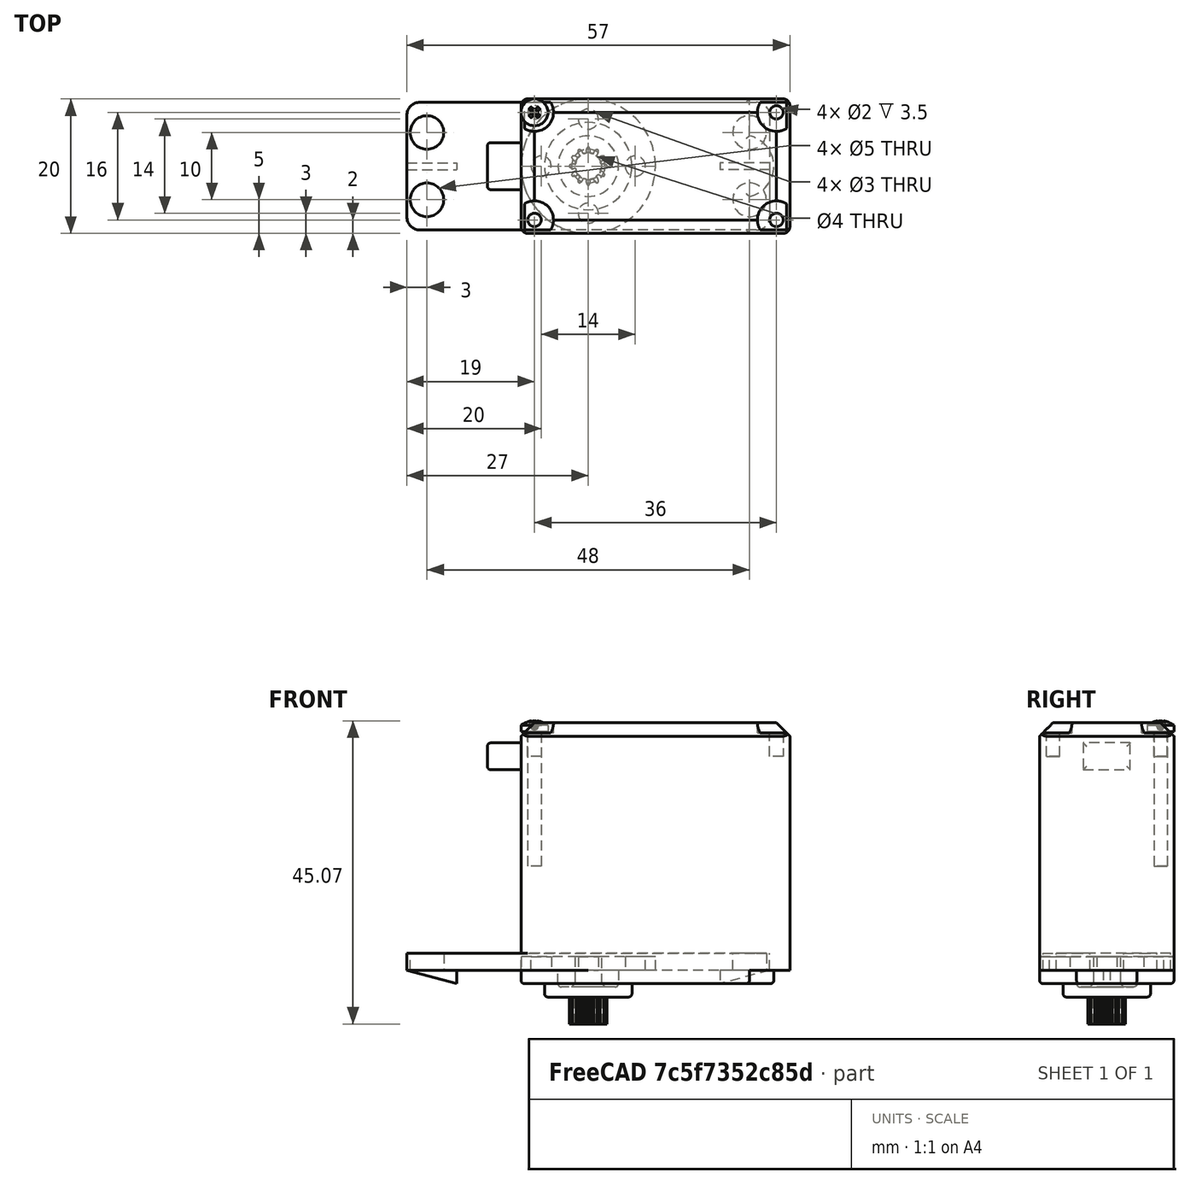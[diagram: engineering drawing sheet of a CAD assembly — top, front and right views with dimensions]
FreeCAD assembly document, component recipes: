
FREECAD ASSEMBLY — COMPONENT RECIPES ("Servo")

This assembly document has 3 components, labeled P0..P2 below (a component is one placed body or linked part). 3 of them carry a construction recipe — the FreeCAD feature program that regenerates the part from scratch, quoted from this document or its linked companion documents; the rest are supplied as boundary geometry only. No exploded tour is included for this assembly.
COMPONENT P0 — recipe-attached ("Hang", modeled in this document).
Construction recipe (the document's own serialized feature program — sketch geometry with constraints, then the solid features built on it; lengths are millimeters unless a unit is written):

FEATURE [PartDesign::CoordinateSystem] LCS_0002
  AttacherType = Attacher::AttachEngine3D
  MapMode = 2
  Support = -> [X_Axis002]
FEATURE [Sketcher::SketchObject] Sketch008
  FullyConstrained = true
  MapMode = 5
  Support = -> [XY_Plane002]
  sketch-geometry (4):
    g0: LineSegment StartX=-27 StartY=9.5 StartZ=0 EndX=27 EndY=9.5 EndZ=0
    g1: LineSegment StartX=27 StartY=9.5 StartZ=0 EndX=27 EndY=-9.5 EndZ=0
    g2: LineSegment StartX=27 StartY=-9.5 StartZ=0 EndX=-27 EndY=-9.5 EndZ=0
    g3: LineSegment StartX=-27 StartY=-9.5 StartZ=0 EndX=-27 EndY=9.5 EndZ=0
  constraints (11):
    c: Coincident(g0,g1)
    c: Coincident(g1,g2)
    c: Coincident(g2,g3)
    c: Coincident(g3,g0)
    c: Horizontal(g0)
    c: Horizontal(g2)
    c: Vertical(g1)
    c: Vertical(g3)
    c: Symmetric(g0,g1,g-1)
    c: Distance(g0) = 54
    c: Distance(g1) = 19
FEATURE [PartDesign::Pad] Pad006
  Direction = (1,1,1)
  Length = 2.5
  Length2 = 100
  Profile = -> Sketch008
  Type = 0
FEATURE [Sketcher::SketchObject] Sketch009
  FullyConstrained = true
  MapMode = 5
  Placement = pos=(0,0,2.5) rot=(0,0,1;0rad)
  Support = -> [Pad006]
  sketch-geometry (8):
    g0: LineSegment StartX=-24 StartY=5 StartZ=0 EndX=24 EndY=5 EndZ=0
    g1: LineSegment StartX=24 StartY=5 StartZ=0 EndX=24 EndY=-5 EndZ=0
    g2: LineSegment StartX=24 StartY=-5 StartZ=0 EndX=-24 EndY=-5 EndZ=0
    g3: LineSegment StartX=-24 StartY=-5 StartZ=0 EndX=-24 EndY=5 EndZ=0
    g4: Circle CenterX=-24 CenterY=5 CenterZ=0 NormalX=0 NormalY=0 NormalZ=1 AngleXU=0 Radius=2.5
    g5: Circle CenterX=24 CenterY=5 CenterZ=0 NormalX=0 NormalY=0 NormalZ=1 AngleXU=0 Radius=2.5
    g6: Circle CenterX=24 CenterY=-5 CenterZ=0 NormalX=0 NormalY=0 NormalZ=1 AngleXU=0 Radius=2.5
    g7: Circle CenterX=-24 CenterY=-5 CenterZ=0 NormalX=0 NormalY=0 NormalZ=1 AngleXU=0 Radius=2.5
  constraints (19):
    c: Coincident(g0,g1)
    c: Coincident(g1,g2)
    c: Coincident(g2,g3)
    c: Coincident(g3,g0)
    c: Horizontal(g0)
    c: Horizontal(g2)
    c: Vertical(g1)
    c: Vertical(g3)
    c: Symmetric(g0,g1,g-1)
    c: Distance(g0) = 48
    c: Distance(g1) = 10
    c: Coincident(g4,g0)
    c: Coincident(g5,g0)
    c: Coincident(g6,g1)
    c: Coincident(g7,g2)
    c: Diameter(g4) = 5
    c: Diameter(g5) = 5
    c: Diameter(g6) = 5
    c: Diameter(g7) = 5
FEATURE [PartDesign::Pocket] Pocket002
  BaseFeature = -> Pad006
  Length = 5
  Length2 = 100
  Profile = -> Sketch009
  Type = 1
FEATURE [PartDesign::Fillet] Fillet007
  Base = -> Pocket002 [Edge2]
  BaseFeature = -> Pocket002
  Radius = 2
  SupportTransform = false
FEATURE [PartDesign::Fillet] Fillet008
  Base = -> Fillet007 [Edge3]
  BaseFeature = -> Fillet007
  Radius = 2
  SupportTransform = false
FEATURE [PartDesign::Fillet] Fillet009
  Base = -> Fillet008 [Edge25]
  BaseFeature = -> Fillet008
  Radius = 2
  SupportTransform = false
FEATURE [PartDesign::Fillet] Fillet010
  Base = -> Fillet009 [Edge19]
  BaseFeature = -> Fillet009
  Radius = 2
  SupportTransform = false
FEATURE [Sketcher::SketchObject] Sketch010
  ExternalGeometry = -> [Fillet010]
  FullyConstrained = true
  MapMode = 5
  Placement = pos=(0,0,0) rot=(1,0,0;1.5708rad)
  Support = -> [XZ_Plane002]
  sketch-geometry (3):
    g0: LineSegment StartX=-27 StartY=0 StartZ=0 EndX=-19.6 EndY=0 EndZ=0
    g1: LineSegment StartX=-19.6 StartY=0 StartZ=0 EndX=-19.6 EndY=-2 EndZ=0
    g2: LineSegment StartX=-27 StartY=0 StartZ=0 EndX=-19.6 EndY=-2 EndZ=0
  constraints (9):
    c: PointOnObject(g0,g-1)
    c: Horizontal(g0)
    c: Vertical(g1)
    c: Coincident(g2,g0)
    c: Coincident(g2,g1)
    c: Distance(g1) = 2
    c: Distance(g0) = 7.4
    c: Coincident(g0,g1)
    c: DistanceX(g-3,g0) = 0
FEATURE [PartDesign::Pad] Pad007
  BaseFeature = -> Fillet010
  Direction = (1,1,1)
  Length = 1
  Length2 = 100
  Midplane = true
  Profile = -> Sketch010
  Type = 0
FEATURE [PartDesign::Mirrored] Mirrored
  BaseFeature = -> Pad007
  MirrorPlane = -> Sketch010 [V_Axis]
  Originals = -> [Pad007]
FEATURE [PartDesign::Body] Body_2  label="Body001"
  Group = -> [LCS_0002,Sketch008,Pad006,Sketch009,Pocket002,Fillet007,Fillet008,Fillet009,Fillet010,Sketch010,Pad007,Mirrored]
  Origin = -> Origin002
  Tip = -> Mirrored
COMPONENT P1 — recipe-attached ("Servo", modeled in this document).
Construction recipe (the document's own serialized feature program — sketch geometry with constraints, then the solid features built on it; lengths are millimeters unless a unit is written):

FEATURE [PartDesign::CoordinateSystem] LCS_0001
  AttacherType = Attacher::AttachEngine3D
  MapMode = 2
  Support = -> [X_Axis001]
FEATURE [Sketcher::SketchObject] Sketch
  FullyConstrained = true
  MapMode = 5
  Support = -> [XY_Plane001]
  sketch-geometry (4):
    g0: LineSegment StartX=-10 StartY=10 StartZ=0 EndX=30 EndY=10 EndZ=0
    g1: LineSegment StartX=30 StartY=10 StartZ=0 EndX=30 EndY=-10 EndZ=0
    g2: LineSegment StartX=30 StartY=-10 StartZ=0 EndX=-10 EndY=-10 EndZ=0
    g3: LineSegment StartX=-10 StartY=-10 StartZ=0 EndX=-10 EndY=10 EndZ=0
  constraints (11):
    c: Coincident(g0,g1)
    c: Coincident(g1,g2)
    c: Coincident(g2,g3)
    c: Coincident(g3,g0)
    c: Horizontal(g0)
    c: Horizontal(g2)
    c: Vertical(g1)
    c: Symmetric(g0,g2,g-1)
    c: Distance(g0) = 40
    c: Distance(g1) = 20
    c: DistanceX(g0,g-1) = 10
FEATURE [PartDesign::Pad] Pad
  Direction = (1,1,1)
  Length = 36.8
  Length2 = 100
  Profile = -> Sketch
  Type = 0
FEATURE [PartDesign::Chamfer] Chamfer
  Angle = 45
  Base = -> Pad [Edge4]
  BaseFeature = -> Pad
  ChamferType = 0
  FlipDirection = false
  Size = 2
  Size2 = 1
  SupportTransform = false
FEATURE [PartDesign::Chamfer] Chamfer001
  Angle = 45
  Base = -> Chamfer [Edge15]
  BaseFeature = -> Chamfer
  ChamferType = 0
  FlipDirection = false
  Size = 2
  Size2 = 1
  SupportTransform = false
FEATURE [PartDesign::Chamfer] Chamfer002
  Angle = 45
  Base = -> Chamfer001 [Edge7]
  BaseFeature = -> Chamfer001
  ChamferType = 0
  FlipDirection = false
  Size = 2
  Size2 = 1
  SupportTransform = false
FEATURE [PartDesign::Chamfer] Chamfer003
  Angle = 45
  Base = -> Chamfer002 [Edge3]
  BaseFeature = -> Chamfer002
  ChamferType = 0
  FlipDirection = false
  Size = 2
  Size2 = 1
  SupportTransform = false
FEATURE [Sketcher::SketchObject] Sketch001
  ExternalGeometry = -> [Chamfer003]
  FullyConstrained = true
  MapMode = 5
  Placement = pos=(0,0,36.8) rot=(0,0,1;0rad)
  Support = -> [Chamfer003]
  sketch-geometry (4):
    g0: Circle CenterX=-8 CenterY=8 CenterZ=0 NormalX=0 NormalY=0 NormalZ=1 AngleXU=0 Radius=2.82843
    g1: Circle CenterX=28 CenterY=8 CenterZ=0 NormalX=0 NormalY=0 NormalZ=1 AngleXU=0 Radius=2.82843
    g2: Circle CenterX=28 CenterY=-8 CenterZ=0 NormalX=0 NormalY=0 NormalZ=1 AngleXU=0 Radius=2.82843
    g3: Circle CenterX=-8 CenterY=-8 CenterZ=0 NormalX=0 NormalY=0 NormalZ=1 AngleXU=0 Radius=2.82843
  constraints (8):
    c: Coincident(g0,g-3)
    c: PointOnObject(g-7,g0)
    c: Coincident(g1,g-6)
    c: Coincident(g2,g-5)
    c: Coincident(g3,g-4)
    c: PointOnObject(g-8,g1)
    c: PointOnObject(g-9,g2)
    c: PointOnObject(g-10,g3)
FEATURE [PartDesign::Pocket] Pocket
  BaseFeature = -> Chamfer003
  Length = 1.5
  Length2 = 100
  Profile = -> Sketch001
  Type = 0
FEATURE [Sketcher::SketchObject] Sketch002
  ExternalGeometry = -> [Pocket]
  FullyConstrained = true
  MapMode = 5
  Placement = pos=(0,0,36.8) rot=(0,0,1;0rad)
  Support = -> [Pocket]
  sketch-geometry (8):
    g0: LineSegment StartX=-8 StartY=8 StartZ=0 EndX=28 EndY=8 EndZ=0
    g1: LineSegment StartX=28 StartY=8 StartZ=0 EndX=28 EndY=-8 EndZ=0
    g2: LineSegment StartX=28 StartY=-8 StartZ=0 EndX=-8 EndY=-8 EndZ=0
    g3: LineSegment StartX=-8 StartY=-8 StartZ=0 EndX=-8 EndY=8 EndZ=0
    g4: Circle CenterX=-8 CenterY=8 CenterZ=0 NormalX=0 NormalY=0 NormalZ=1 AngleXU=0 Radius=1
    g5: Circle CenterX=28 CenterY=8 CenterZ=0 NormalX=0 NormalY=0 NormalZ=1 AngleXU=0 Radius=1
    g6: Circle CenterX=-8 CenterY=-8 CenterZ=0 NormalX=0 NormalY=0 NormalZ=1 AngleXU=0 Radius=1
    g7: Circle CenterX=28 CenterY=-8 CenterZ=0 NormalX=0 NormalY=0 NormalZ=1 AngleXU=0 Radius=1
  constraints (19):
    c: Coincident(g0,g1)
    c: Coincident(g1,g2)
    c: Coincident(g2,g3)
    c: Coincident(g3,g0)
    c: Horizontal(g0)
    c: Horizontal(g2)
    c: Vertical(g1)
    c: Symmetric(g0,g2,g-1)
    c: DistanceY(g-3,g0) = 0
    c: DistanceX(g0,g-4) = 0
    c: DistanceX(g-5,g2) = 0
    c: Coincident(g4,g0)
    c: Coincident(g5,g0)
    c: Coincident(g6,g2)
    c: Coincident(g7,g1)
    c: Diameter(g4) = 2
    c: Diameter(g5) = 2
    c: Diameter(g6) = 2
    c: Diameter(g7) = 2
FEATURE [PartDesign::Pocket] Pocket001
  BaseFeature = -> Pocket
  Length = 5
  Length2 = 100
  Profile = -> Sketch002
  Type = 0
FEATURE [Sketcher::SketchObject] Sketch003
  FullyConstrained = true
  MapMode = 5
  Placement = pos=(0,0,0) rot=(1,0,0;3.14159rad)
  Support = -> [Pocket001]
  sketch-geometry (1):
    g0: Circle CenterX=0 CenterY=0 CenterZ=0 NormalX=0 NormalY=0 NormalZ=1 AngleXU=0 Radius=10
  constraints (2):
    c: Coincident(g0,g-1)
    c: Diameter(g0) = 20
FEATURE [PartDesign::Pad] Pad001
  BaseFeature = -> Pocket001
  Direction = (1,1,1)
  Length = 2
  Length2 = 100
  Profile = -> Sketch003
  Refine = true
  Type = 0
FEATURE [Sketcher::SketchObject] Sketch004
  FullyConstrained = true
  MapMode = 5
  Placement = pos=(0,0,0) rot=(1,0,0;3.14159rad)
  Support = -> [Pad001]
  sketch-geometry (4):
    g0: LineSegment StartX=0 StartY=10 StartZ=0 EndX=24 EndY=10 EndZ=0
    g1: LineSegment StartX=24 StartY=10 StartZ=0 EndX=24 EndY=-10 EndZ=0
    g2: LineSegment StartX=24 StartY=-10 StartZ=0 EndX=0 EndY=-10 EndZ=0
    g3: LineSegment StartX=0 StartY=-10 StartZ=0 EndX=0 EndY=10 EndZ=0
  constraints (11):
    c: Coincident(g0,g1)
    c: Coincident(g1,g2)
    c: Coincident(g2,g3)
    c: Coincident(g3,g0)
    c: Horizontal(g0)
    c: Horizontal(g2)
    c: Vertical(g1)
    c: Symmetric(g0,g2,g-1)
    c: Distance(g0) = 24
    c: Distance(g3) = 20
    c: DistanceX(g0,g-1) = 0
FEATURE [PartDesign::Pad] Pad002
  BaseFeature = -> Pad001
  Direction = (1,1,1)
  Length = 2
  Length2 = 100
  Profile = -> Sketch004
  Refine = true
  Type = 0
FEATURE [Sketcher::SketchObject] Sketch005
  ExternalGeometry = -> [Pad002]
  FullyConstrained = true
  MapMode = 5
  Placement = pos=(0,0,0) rot=(1,0,0;3.14159rad)
  Support = -> [Pad002]
  sketch-geometry (2):
    g0: ArcOfCircle CenterX=23 CenterY=0 CenterZ=0 NormalX=0 NormalY=0 NormalZ=1 AngleXU=0 Radius=4.60977 StartAngle=4.93106 EndAngle=7.63531
    g1: LineSegment StartX=24 StartY=4.5 StartZ=0 EndX=24 EndY=-4.5 EndZ=0
  constraints (7):
    c: PointOnObject(g0,g-1)
    c: PointOnObject(g0,g-3)
    c: PointOnObject(g0,g-3)
    c: DistanceY(g0,g0) = 9
    c: DistanceX(g0,g-3) = 1
    c: Coincident(g1,g0)
    c: Coincident(g1,g0)
FEATURE [PartDesign::Pad] Pad003
  BaseFeature = -> Pad002
  Direction = (1,1,1)
  Length = 2
  Length2 = 100
  Profile = -> Sketch005
  Refine = true
  Type = 0
FEATURE [PartDesign::Fillet] Fillet
  Base = -> Pad003 [Edge40]
  BaseFeature = -> Pad003
  Radius = 1
  SupportTransform = false
FEATURE [PartDesign::Fillet] Fillet001
  Base = -> Fillet [Edge44]
  BaseFeature = -> Fillet
  Radius = 1
  SupportTransform = false
FEATURE [PartDesign::Fillet] Fillet002
  Base = -> Fillet001 [Edge53]
  BaseFeature = -> Fillet001
  Radius = 1
  SupportTransform = false
FEATURE [PartDesign::Fillet] Fillet003
  Base = -> Fillet002 [Edge65]
  BaseFeature = -> Fillet002
  Radius = 1
  SupportTransform = false
FEATURE [PartDesign::Fillet] Fillet004
  Base = -> Fillet003 [Face28]
  BaseFeature = -> Fillet003
  Radius = 0.5
  SupportTransform = false
FEATURE [Sketcher::SketchObject] Sketch006
  FullyConstrained = true
  MapMode = 5
  Placement = pos=(0,0,-2) rot=(1,0,0;3.14159rad)
  Support = -> [Fillet004]
  sketch-geometry (1):
    g0: Circle CenterX=0 CenterY=0 CenterZ=0 NormalX=0 NormalY=0 NormalZ=1 AngleXU=0 Radius=6.5
  constraints (2):
    c: Coincident(g0,g-1)
    c: Diameter(g0) = 13
FEATURE [PartDesign::Pad] Pad004
  BaseFeature = -> Fillet004
  Direction = (1,1,1)
  Length = 2
  Length2 = 100
  Profile = -> Sketch006
  Type = 0
FEATURE [PartDesign::Fillet] Fillet005
  Base = -> Pad004 [Edge96]
  BaseFeature = -> Pad004
  Radius = 0.5
  SupportTransform = false
FEATURE [Sketcher::SketchObject] Sketch007
  ExternalGeometry = -> [Fillet005]
  FullyConstrained = true
  MapMode = 5
  Placement = pos=(-10,0,0) rot=(0.57735,-0.57735,-0.57735;2.0944rad)
  Support = -> [Fillet005]
  sketch-geometry (4):
    g0: LineSegment StartX=-3.5 StartY=33.8 StartZ=0 EndX=3.5 EndY=33.8 EndZ=0
    g1: LineSegment StartX=3.5 StartY=33.8 StartZ=0 EndX=3.5 EndY=29.8 EndZ=0
    g2: LineSegment StartX=3.5 StartY=29.8 StartZ=0 EndX=-3.5 EndY=29.8 EndZ=0
    g3: LineSegment StartX=-3.5 StartY=29.8 StartZ=0 EndX=-3.5 EndY=33.8 EndZ=0
  constraints (11):
    c: Coincident(g0,g1)
    c: Coincident(g1,g2)
    c: Coincident(g2,g3)
    c: Coincident(g3,g0)
    c: Horizontal(g2)
    c: Vertical(g1)
    c: Vertical(g3)
    c: Symmetric(g0,g0,g-2)
    c: DistanceY(g2,g-3) = 7
    c: Distance(g1) = 4
    c: Distance(g0) = 7
FEATURE [PartDesign::Pad] Pad005
  BaseFeature = -> Fillet005
  Direction = (1,1,1)
  Length = 5
  Length2 = 100
  Profile = -> Sketch007
  Type = 0
FEATURE [PartDesign::Fillet] Fillet006
  Base = -> Pad005 [Face47]
  BaseFeature = -> Pad005
  Radius = 0.5
  SupportTransform = false
FEATURE [PartDesign::Body] Body
  Group = -> [LCS_0001,Sketch,Pad,Chamfer,Chamfer001,Chamfer002,Chamfer003,Sketch001,Pocket,Sketch002,Pocket001,Sketch003,Pad001,Sketch004,Pad002,Sketch005,Pad003,Fillet,Fillet001,Fillet002,Fillet003,Fillet004,Sketch006,Pad004,Fillet005,Sketch007,Pad005,Fillet006]
  Origin = -> Origin001
  Tip = -> Fillet006
COMPONENT P2 — recipe-attached ("ServoWheel", modeled in this document).
Construction recipe (the document's own serialized feature program — sketch geometry with constraints, then the solid features built on it; lengths are millimeters unless a unit is written):

FEATURE [PartDesign::CoordinateSystem] LCS_0004
  AttacherType = Attacher::AttachEngine3D
  MapMode = 2
  Support = -> [X_Axis005]
FEATURE [Sketcher::SketchObject] Sketch011
  FullyConstrained = true
  MapMode = 5
  Support = -> [XY_Plane005]
  sketch-geometry (1):
    g0: Circle CenterX=0 CenterY=0 CenterZ=0 NormalX=0 NormalY=0 NormalZ=1 AngleXU=0 Radius=10
  constraints (2):
    c: Coincident(g0,g-1)
    c: Diameter(g0) = 20
FEATURE [PartDesign::Pad] Pad008
  Direction = (1,1,1)
  Length = 2
  Length2 = 100
  Profile = -> Sketch011
  Type = 0
FEATURE [Sketcher::SketchObject] Sketch012
  FullyConstrained = true
  MapMode = 5
  Placement = pos=(0,0,0) rot=(1,0,0;3.14159rad)
  Support = -> [Pad008]
  sketch-geometry (1):
    g0: Circle CenterX=0 CenterY=0 CenterZ=0 NormalX=0 NormalY=0 NormalZ=1 AngleXU=0 Radius=4.5
  constraints (2):
    c: Coincident(g0,g-1)
    c: Diameter(g0) = 9
FEATURE [PartDesign::Pad] Pad009
  BaseFeature = -> Pad008
  Direction = (1,1,1)
  Length = 2.5
  Length2 = 100
  Profile = -> Sketch012
  Type = 0
FEATURE [Sketcher::SketchObject] Sketch013
  FullyConstrained = true
  MapMode = 5
  Placement = pos=(0,0,-2.5) rot=(1,0,0;3.14159rad)
  Support = -> [Pad009]
  sketch-geometry (1):
    g0: Circle CenterX=0 CenterY=0 CenterZ=0 NormalX=0 NormalY=0 NormalZ=1 AngleXU=0 Radius=2
  constraints (2):
    c: Coincident(g0,g-1)
    c: Diameter(g0) = 4
FEATURE [PartDesign::Pocket] Pocket003
  BaseFeature = -> Pad009
  Length = 5
  Length2 = 100
  Profile = -> Sketch013
  Type = 1
FEATURE [PartDesign::Chamfer] Chamfer004
  Angle = 45
  Base = -> Pocket003 [Edge8]
  BaseFeature = -> Pocket003
  ChamferType = 0
  FlipDirection = false
  Size = 0.5
  Size2 = 1
  SupportTransform = false
FEATURE [PartDesign::Fillet] Fillet011
  Base = -> Chamfer004 [Edge7]
  BaseFeature = -> Chamfer004
  Radius = 0.5
  SupportTransform = false
FEATURE [Sketcher::SketchObject] Sketch014
  FullyConstrained = true
  MapMode = 5
  Placement = pos=(0,0,0) rot=(1,0,0;3.14159rad)
  Support = -> [Fillet011]
  sketch-geometry (2):
    g0: Circle CenterX=0 CenterY=0 CenterZ=0 NormalX=0 NormalY=0 NormalZ=1 AngleXU=0 Radius=7
    g1: Circle CenterX=7 CenterY=0 CenterZ=0 NormalX=0 NormalY=0 NormalZ=1 AngleXU=0 Radius=1.5
  constraints (5):
    c: Coincident(g0,g-1)
    c: Diameter(g0) = 14
    c: PointOnObject(g1,g0)
    c: Diameter(g1) = 3
    c: PointOnObject(g1,g-1)
FEATURE [PartDesign::Pocket] Pocket004
  BaseFeature = -> Fillet011
  Length = 5
  Length2 = 100
  Profile = -> Sketch014
  Type = 1
FEATURE [PartDesign::PolarPattern] PolarPattern
  Angle = 360
  Axis = -> Sketch014 [N_Axis]
  BaseFeature = -> Pocket004
  Occurrences = 4
  Originals = -> [Pocket004]
FEATURE [PartDesign::Body] Body_3
  Group = -> [LCS_0004,Sketch011,Pad008,Sketch012,Pad009,Sketch013,Pocket003,Chamfer004,Fillet011,Sketch014,Pocket004,PolarPattern]
  Origin = -> Origin005
  Tip = -> PolarPattern
PROVENANCE & LICENSES
A FreeCAD (.FCStd) document from a public repository crawl; recipes are the document's own serialized feature recipes (and, for linked parts, companion documents' recipes).
License: mit.
